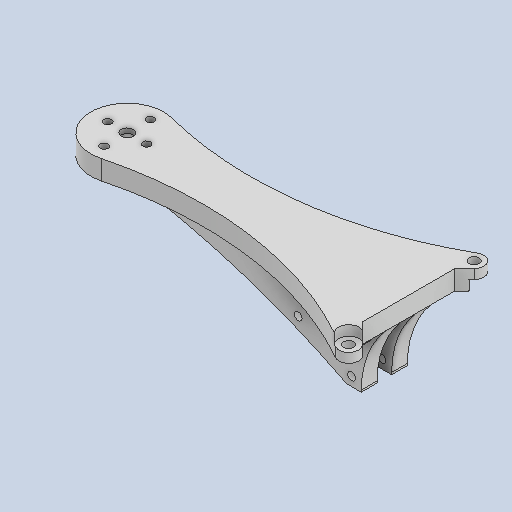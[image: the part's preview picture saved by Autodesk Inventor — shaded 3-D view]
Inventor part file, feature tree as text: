
AUTODESK INVENTOR PART (.ipt)
format: ipt  version: 2025.2 (Build 292293000, 293)  size: 261,120 bytes
history: native  units: mm
features: extrude x11, sketch x4, chamfer x1
ambient origin geometry x8: Origin, YZ Plane, XZ Plane, XY Plane, X Axis, Y Axis, Z Axis, Center Point
bodies: Solid1 (feature_tree)
feature tree (16):
  sketch  "Sketch1"  dims[d1=9.5mm d2=3.2mm]
  extrude  "Extrusion1"  Depth=3.2mm
  extrude  "Extrusion2"  Depth=8.0mm
  extrude  "Extrusion3"  Depth=8.0mm TaperAngle=0.0deg
  extrude  "Extrusion9"  Depth=3.9mm TaperAngle=0.0deg
  sketch  "Sketch2"  dims[d3=3.2mm d4=8.0mm]
  extrude  "Extrusion4"  Depth=290.0mm
  extrude  "Extrusion11"  Depth=2.0mm
  extrude  "Extrusion12"  Depth=6.0mm
  sketch  "Sketch10"  dims[d12=3.9mm d13=0.0mm d14=3.9mm d15=0.0mm d16=290.0mm d17=85.0mm d18=6.0mm d19=30.0mm d20=19.0mm d21=0.0mm d55=5.0mm d56=2.0mm d57=0.0mm d61=6.0mm d62=0.0mm d63=3.7mm d64=3.2mm d65=4.0mm d67=8.0mm d68=4.0mm d69=4.2mm d70=150.0mm d71=3.2mm d72=294.5mm d73=26.0mm d75=3.2mm d76=6.5mm d77=0.0mm d78=0.0mm d79=10.0mm d80=40.0mm d82=10.0mm d84=38.0mm d85=105.962948mm d86=4.25mm d101=5.2mm d102=7.5mm d109=25.0mm d110=0.0mm d111=21.0mm d112=0.0mm d113=10.0mm d114=0.0mm d115=6.0mm d116=0.0mm d117=1.5mm d118=2.0mm d119=45.0deg d44=0.5mm d45=0.872665mm d46=0.5mm d47=0.872665mm]
  extrude  "Extrusion16"  Depth=2.0mm
  extrude  "Extrusion17"  Depth=19.0mm TaperAngle=0.0deg
  extrude  "Extrusion18"  Depth=2.0mm
  extrude  "Extrusion19"  Depth=2.0mm TaperAngle=0.0deg
  chamfer  "Chamfer1"  Distance=6.0mm
  sketch  "Sketch9"  dims[d5=30.0mm d10=8.0mm d11=0.0mm]
